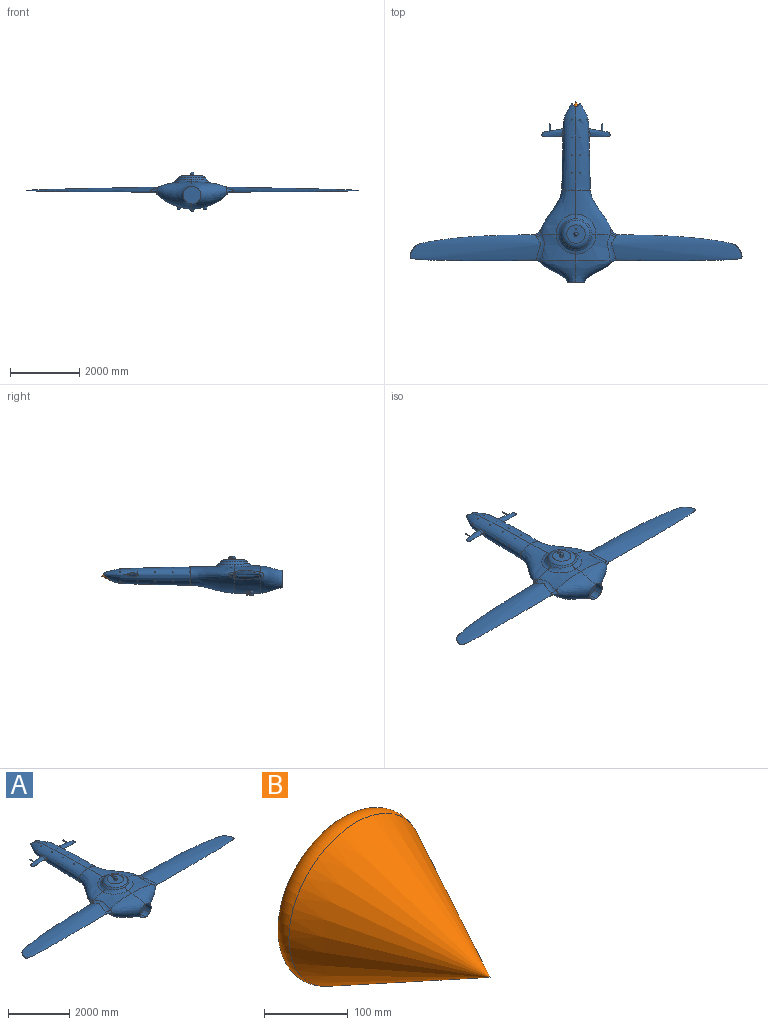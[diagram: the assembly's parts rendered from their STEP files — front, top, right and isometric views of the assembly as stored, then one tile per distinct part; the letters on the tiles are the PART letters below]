
ASSEMBLY  parts=2 mates=1
PART A: 189 faces, bbox 13589.5x5179.7x1155.7 mm
  f0: bspline ~2509.88x526.8mm, area 2318392.8mm2, adj f1,f116,f117,f118,f119,f120,f122,f164
  f1: cylinder r=12.7mm len=106.09mm, axis (0,0,1), area 7616mm2, adj f0,f2,f116,f119
  f2: cylinder r=12.7mm len=254mm, axis (-1,0,0), area 19047.2mm2, adj f1,f3,f114,f115
  f3: cylinder r=12.7mm len=254mm, axis (0,0,1), area 19047.2mm2, adj f2,f4,f112,f113
  f4: cylinder r=12.7mm len=254mm, axis (-1,0,0), area 20268.3mm2, adj f3,f5,f114,f118
  f5: cylinder r=12.7mm len=144.03mm, axis (0,0,1), area 10744mm2, adj f4,f6,f112,f122
  f6: bspline ~1270x1036.44mm, area 1946385.1mm2, adj f5,f7,f89,f90,f91,f92,f93,f94
  f7: bspline ~588.86x581.18mm, area 123308.8mm2, adj f6,f8,f65,f66
  f8: bspline ~588.86x581.18mm, area 123308.8mm2, adj f7,f9,f66,f119
  f9: bspline ~618.36x584.85mm, area 126946.2mm2, adj f8,f10,f65,f66
  f10: extruded ~985.62x762mm, area 505885mm2, adj f9,f11,f54,f89,f119
  f11: bspline ~792.27x241.93mm, area 105491.6mm2, adj f10,f12,f52,f53
  f12: bspline ~183.5x140.7mm, area 9732.5mm2, adj f11,f13,f53,f119
  f13: bspline ~246.9x202.36mm, area 17719.5mm2, adj f12,f14,f53,f119
  f14: bspline ~241.81x196.61mm, area 19710.9mm2, adj f13,f15,f53,f119
  f15: bspline ~211.13x111.05mm, area 6367.3mm2, adj f14,f16,f53,f119
  f16: bspline ~788.4x224mm, area 161750.4mm2, adj f15,f17,f52,f53
  f17: extruded ~995.01x762mm, area 844105.4mm2, adj f16,f18,f35,f54,f94,f119
  f18: sphere r=50.8mm, area 23373mm2, adj f17,f19,f23,f27,f31
  f19: cylinder r=12.7mm len=108.81mm, axis (0,1,0), area 8156.4mm2, adj f18,f20
  f20: torus R=6.35mm, axis (0,-1,0), area 651.3mm2, adj f19,f21
  f21: cylinder r=6.35mm len=110.15mm, axis (0,1,0), area 4270.5mm2, adj f20,f22
  f22: sphere r=50.8mm, area 141.2mm2, adj f21
  f23: cylinder r=12.7mm len=110.32mm, axis (0,1,0), area 8224.9mm2, adj f18,f24
  f24: torus R=6.35mm, axis (0,-1,0), area 651.3mm2, adj f23,f25
  f25: cylinder r=6.35mm len=111.23mm, axis (0,1,0), area 4302.2mm2, adj f24,f26
  f26: sphere r=50.8mm, area 143.8mm2, adj f25
  f27: cylinder r=12.7mm len=104.3mm, axis (0,1,0), area 8323mm2, adj f18,f28
  f28: torus R=6.35mm, axis (0,-1,0), area 651.3mm2, adj f27,f29
  f29: cylinder r=6.35mm len=105.08mm, axis (0,1,0), area 4192.6mm2, adj f28,f30
  f30: sphere r=50.8mm, area 134.4mm2, adj f29
  f31: cylinder r=12.7mm len=105.74mm, axis (0,1,0), area 8437.9mm2, adj f18,f32
  f32: torus R=6.35mm, axis (0,-1,0), area 651.3mm2, adj f31,f33
  f33: cylinder r=6.35mm len=107.99mm, axis (0,1,0), area 4208.2mm2, adj f32,f34
  f34: sphere r=50.8mm, area 136.5mm2, adj f33
  f35: sphere r=50.8mm, area 24215.9mm2, adj f17,f36,f40,f44,f48,f94
  f36: cylinder r=12.7mm len=112.81mm, axis (0,-1,0), area 8336.5mm2, adj f35,f37
  f37: torus R=6.35mm, axis (0,-1,0), area 651.3mm2, adj f36,f38
  f38: cylinder r=6.35mm len=112.95mm, axis (0,-1,0), area 4353.5mm2, adj f37,f39
  f39: sphere r=50.8mm, area 146.5mm2, adj f38
  f40: cylinder r=12.7mm len=112.81mm, axis (0,-1,0), area 8337.9mm2, adj f35,f41
  f41: torus R=6.35mm, axis (0,-1,0), area 651.3mm2, adj f40,f42
  f42: cylinder r=6.35mm len=112.95mm, axis (0,-1,0), area 4353.5mm2, adj f41,f43
  f43: sphere r=50.8mm, area 146.5mm2, adj f42
  f44: cylinder r=12.7mm len=103.69mm, axis (0,-1,0), area 7933.1mm2, adj f35,f45
  f45: torus R=6.35mm, axis (0,-1,0), area 651.3mm2, adj f44,f46
  f46: cylinder r=6.35mm len=106.47mm, axis (0,-1,0), area 4166.3mm2, adj f45,f47
  f47: sphere r=50.8mm, area 132mm2, adj f46
  f48: cylinder r=12.7mm len=103.69mm, axis (0,-1,0), area 7932.9mm2, adj f35,f49
  f49: torus R=6.35mm, axis (0,-1,0), area 651.3mm2, adj f48,f50
  f50: cylinder r=6.35mm len=105.21mm, axis (0,-1,0), area 4164.8mm2, adj f49,f51
  f51: sphere r=50.8mm, area 131.6mm2, adj f50
  f52: bspline ~219.13x194.66mm, area 35350.9mm2, adj f11,f16,f53,f54
  f53: bspline ~6257.94x1180.14mm, area 4844157.5mm2, adj f11,f12,f13,f14,f15,f16,f52
  f54: bspline ~1036.35x785.31mm, area 1162564.2mm2, adj f10,f17,f52,f55,f59,f60
  f55: extruded ~254x186.24mm, area 53098mm2, adj f54,f56,f58,f59
  f56: plane 508x508mm, normal (0,-1,0), area 202688.6mm2, adj f55,f57,f58,f59
  f57: extruded ~426.72x254mm, area 149586.4mm2, adj f56,f58,f59,f60
  f58: extruded ~254x186.24mm, area 53097.8mm2, adj f55,f56,f57,f60
  f59: extruded ~426.72x254mm, area 149583.4mm2, adj f54,f55,f56,f57
  f60: bspline ~1036.35x785.31mm, area 1162564.2mm2, adj f54,f57,f58,f61,f89,f94
  f61: bspline ~219.13x194.66mm, area 35346.5mm2, adj f60,f62,f63,f64
  f62: bspline ~808.62x242.2mm, area 105497.7mm2, adj f61,f63,f89,f90
  f63: bspline ~6257.95x1180.14mm, area 4845672.1mm2, adj f61,f62,f64,f90,f91,f92,f93
  f64: bspline ~782.08x223.3mm, area 161757.5mm2, adj f61,f63,f93,f94
  f65: bspline ~618.36x584.03mm, area 126947.2mm2, adj f7,f9,f66,f89
  f66: sphere r=539.36mm, area 214399.3mm2, adj f7,f8,f9,f65,f67
  f67: torus R=266.46mm, axis (0,0,1), area 311016.1mm2, adj f66,f68
  f68: plane 532.92x532.92mm, normal (0,0,1), area 210384.4mm2, adj f67,f69
  f69: cylinder r=63.5mm len=127mm, axis (0,0,-1), area 86.1mm2, adj f68,f70
  f70: torus R=38.1mm, axis (0,0,1), area 13604.9mm2, adj f69,f71
  f71: plane 76.2x76.2mm, normal (0,0,1), area 257.2mm2, adj f70,f72
  f72: sphere r=50.8mm, area 25095mm2, adj f71,f73,f77,f81,f85
  f73: cylinder r=12.7mm len=106.26mm, axis (0,-1,0), area 8044.5mm2, adj f72,f74
  f74: torus R=6.35mm, axis (0,-1,0), area 651.3mm2, adj f73,f75
  f75: cylinder r=6.35mm len=108.31mm, axis (0,-1,0), area 4234.8mm2, adj f74,f76
  f76: sphere r=50.8mm, area 137.2mm2, adj f75
  f77: cylinder r=12.7mm len=106.26mm, axis (0,-1,0), area 8043.8mm2, adj f72,f78
  f78: torus R=6.35mm, axis (0,-1,0), area 651.3mm2, adj f77,f79
  f79: cylinder r=6.35mm len=108.31mm, axis (0,-1,0), area 4234.8mm2, adj f78,f80
  f80: sphere r=50.8mm, area 137.2mm2, adj f79
  f81: cylinder r=12.7mm len=107.75mm, axis (0,-1,0), area 8105.8mm2, adj f72,f82
  f82: torus R=6.35mm, axis (0,-1,0), area 651.3mm2, adj f81,f83
  f83: cylinder r=6.35mm len=109.39mm, axis (0,-1,0), area 4247.9mm2, adj f82,f84
  f84: sphere r=50.8mm, area 138.5mm2, adj f83
  f85: cylinder r=12.7mm len=107.75mm, axis (0,-1,0), area 8107.9mm2, adj f72,f86
  f86: torus R=6.35mm, axis (0,-1,0), area 651.3mm2, adj f85,f87
  f87: cylinder r=6.35mm len=109.39mm, axis (0,-1,0), area 4248.2mm2, adj f86,f88
  f88: sphere r=50.8mm, area 139.2mm2, adj f87
  f89: extruded ~985.62x762mm, area 505886.1mm2, adj f6,f10,f60,f62,f65
  f90: bspline ~184.63x142.86mm, area 9732.3mm2, adj f6,f62,f63,f91
  f91: bspline ~246.9x202.37mm, area 17719.8mm2, adj f6,f63,f90,f92
  f92: bspline ~241.81x196.61mm, area 19710.7mm2, adj f6,f63,f91,f93
  f93: bspline ~209.2x108.48mm, area 6366.9mm2, adj f6,f63,f64,f92
  f94: extruded ~995.01x762mm, area 838596.6mm2, adj f6,f17,f35,f60,f64,f95
  f95: sphere r=50.8mm, area 23112.9mm2, adj f94,f96,f100,f104,f108
  f96: cylinder r=12.7mm len=107.49mm, axis (0,1,0), area 8096.8mm2, adj f95,f97
  f97: torus R=6.35mm, axis (0,-1,0), area 651.3mm2, adj f96,f98
  f98: cylinder r=6.35mm len=109.2mm, axis (0,1,0), area 4242.8mm2, adj f97,f99
  f99: sphere r=50.8mm, area 139.1mm2, adj f98
  f100: cylinder r=12.7mm len=112.33mm, axis (0,1,0), area 8316.2mm2, adj f95,f101
  f101: torus R=6.35mm, axis (0,-1,0), area 651.3mm2, adj f100,f102
  f102: cylinder r=6.35mm len=112.66mm, axis (0,1,0), area 4344.3mm2, adj f101,f103
  f103: sphere r=50.8mm, area 147.3mm2, adj f102
  f104: cylinder r=12.7mm len=107.56mm, axis (0,1,0), area 8583.2mm2, adj f95,f105
  f105: torus R=6.35mm, axis (0,-1,0), area 651.3mm2, adj f104,f106
  f106: cylinder r=6.35mm len=109.38mm, axis (0,1,0), area 4248.1mm2, adj f105,f107
  f107: sphere r=50.8mm, area 139.5mm2, adj f106
  f108: cylinder r=12.7mm len=102.97mm, axis (0,1,0), area 7903mm2, adj f95,f109
  f109: torus R=6.35mm, axis (0,-1,0), area 651.3mm2, adj f108,f110
  f110: cylinder r=6.35mm len=105.95mm, axis (0,1,0), area 4151.9mm2, adj f109,f111
  f111: sphere r=50.8mm, area 132.5mm2, adj f110
  f112: cylinder r=12.7mm len=268.02mm, axis (-1,0,0), area 20180.1mm2, adj f3,f5,f6,f122
  f113: cylinder r=12.7mm len=207.13mm, axis (-1,0,0), area 14835.5mm2, adj f3,f6,f115,f122
  f114: cylinder r=12.7mm len=254mm, axis (0,0,1), area 19047.2mm2, adj f2,f4,f116,f117
  f115: cylinder r=12.7mm len=106.09mm, axis (0,0,1), area 7616mm2, adj f2,f6,f113,f122
  f116: cylinder r=12.7mm len=207.13mm, axis (-1,0,0), area 14904.7mm2, adj f0,f1,f114,f119
  f117: cylinder r=12.7mm len=268.02mm, axis (-1,0,0), area 20180.1mm2, adj f0,f114,f118,f119
  f118: cylinder r=12.7mm len=144.03mm, axis (0,0,1), area 10744mm2, adj f0,f4,f117,f119
  f119: bspline ~1270x1036.44mm, area 1946422mm2, adj f0,f1,f6,f8,f10,f12,f13,f14
  f120: cylinder r=127mm len=404.44mm, axis (0,1,0), area 238128.3mm2, adj f0,f121,f122
  f121: plane 254x254mm, normal (0,1,0), area 50670.7mm2, adj f120
  f122: bspline ~2512.68x526.8mm, area 2314098.8mm2, adj f0,f5,f6,f112,f113,f115,f120,f123
  f123: cylinder r=12.7mm len=237.09mm, axis (-1,0,0), area 17739.1mm2, adj f122,f124,f159
  f124: cylinder r=12.7mm len=254mm, axis (0,0,1), area 19047.2mm2, adj f123,f125,f127,f154
  f125: cylinder r=12.7mm len=254mm, axis (-1,0,0), area 19047.2mm2, adj f124,f126,f158,f165
  f126: cylinder r=12.7mm len=254mm, axis (0,0,1), area 19047.2mm2, adj f125,f127,f168,f183
  f127: cylinder r=12.7mm len=254mm, axis (-1,0,0), area 19047.2mm2, adj f124,f126,f159,f187
  f128: cylinder r=12.7mm len=258.69mm, axis (-1,0,0), area 19559.6mm2, adj f122,f129,f163
  f129: cylinder r=12.7mm len=254mm, axis (0,0,1), area 19047.2mm2, adj f128,f130,f132,f138
  f130: cylinder r=12.7mm len=254mm, axis (-1,0,0), area 19047.2mm2, adj f129,f131,f162,f167
  f131: cylinder r=12.7mm len=254mm, axis (0,0,1), area 19047.2mm2, adj f130,f132,f169,f171
  f132: cylinder r=12.7mm len=254mm, axis (-1,0,0), area 19047.2mm2, adj f129,f131,f163,f185
  f133: cylinder r=12.7mm len=107.69mm, axis (-1,0,0), area 6456.4mm2, adj f122,f134,f156
  f134: cylinder r=12.7mm len=254mm, axis (0,0,1), area 19047.2mm2, adj f133,f135,f137,f148
  f135: cylinder r=12.7mm len=254mm, axis (-1,0,0), area 19047.2mm2, adj f134,f136,f156,f164
  f136: cylinder r=12.7mm len=254mm, axis (0,0,1), area 19047.2mm2, adj f135,f137,f170,f181
  f137: cylinder r=12.7mm len=254mm, axis (-1,0,0), area 19047.2mm2, adj f134,f136,f157,f188
  f138: cylinder r=12.7mm len=202.09mm, axis (-1,0,0), area 14521.6mm2, adj f122,f129,f162
  f139: bspline ~295.03x108.05mm, area 31421mm2, adj f122,f140,f146,f147
  f140: bspline ~1015.9x358.87mm, area 200607.7mm2, adj f139,f141,f142,f146,f147
  f141: torus R=7.62mm, axis (0,1,0), area 1528.2mm2, adj f140,f142
  f142: cylinder r=12.7mm len=255.27mm, axis (0,-1,0), area 17606.1mm2, adj f140,f141,f143
  f143: torus R=6.35mm, axis (0,1,0), area 651.3mm2, adj f142,f144
  f144: cylinder r=6.35mm len=139.7mm, axis (0,-1,0), area 5573.8mm2, adj f143,f145
  f145: plane 12.7x12.7mm, normal (0,1,0), area 126.7mm2, adj f144
  f146: bspline ~56.61x55.15mm, area 1675mm2, adj f122,f139,f140,f147
  f147: bspline ~59.44x54.97mm, area 1492mm2, adj f122,f139,f140,f146
  f148: cylinder r=12.7mm len=205.31mm, axis (-1,0,0), area 14745.6mm2, adj f122,f134,f157
  f149: cylinder r=12.7mm len=189.58mm, axis (-1,0,0), area 13488mm2, adj f122,f150,f160
  f150: cylinder r=12.7mm len=254mm, axis (0,0,1), area 19047.2mm2, adj f149,f151,f153,f155
  f151: cylinder r=12.7mm len=254mm, axis (-1,0,0), area 19047.2mm2, adj f150,f152,f160,f166
  f152: cylinder r=12.7mm len=254mm, axis (0,0,1), area 19047.2mm2, adj f151,f153,f182,f184
  f153: cylinder r=12.7mm len=254mm, axis (-1,0,0), area 19047.2mm2, adj f150,f152,f161,f186
  f154: cylinder r=12.7mm len=164.58mm, axis (-1,0,0), area 11356.2mm2, adj f122,f124,f158
  f155: cylinder r=12.7mm len=249.54mm, axis (-1,0,0), area 18836mm2, adj f122,f150,f161
  f156: cylinder r=12.7mm len=48.26mm, axis (0,0,1), area 3275.4mm2, adj f122,f133,f135
  f157: cylinder r=12.7mm len=87.14mm, axis (0,0,1), area 6446.9mm2, adj f122,f137,f148
  f158: cylinder r=12.7mm len=82.06mm, axis (0,0,1), area 5971.9mm2, adj f122,f125,f154
  f159: cylinder r=12.7mm len=116.5mm, axis (0,0,1), area 8789.2mm2, adj f122,f123,f127
  f160: cylinder r=12.7mm len=98.91mm, axis (0,0,1), area 7316.3mm2, adj f122,f149,f151
  f161: cylinder r=12.7mm len=133.64mm, axis (0,0,1), area 10157mm2, adj f122,f153,f155
  f162: cylinder r=12.7mm len=106.77mm, axis (0,0,1), area 7943.9mm2, adj f122,f130,f138
  f163: cylinder r=12.7mm len=142.71mm, axis (0,0,1), area 10881.3mm2, adj f122,f128,f132
  f164: cylinder r=12.7mm len=39.21mm, axis (0,0,1), area 2553mm2, adj f0,f135,f170
  f165: cylinder r=12.7mm len=75.14mm, axis (0,0,1), area 5419.9mm2, adj f0,f125,f183
  f166: cylinder r=12.7mm len=92.76mm, axis (0,0,1), area 6825.7mm2, adj f0,f151,f182
  f167: cylinder r=12.7mm len=100.52mm, axis (0,0,1), area 7445mm2, adj f0,f130,f171
  f168: cylinder r=12.7mm len=237.99mm, axis (-1,0,0), area 17808.6mm2, adj f0,f126,f187
  f169: cylinder r=12.7mm len=260.83mm, axis (-1,0,0), area 19725.9mm2, adj f0,f131,f185
  f170: cylinder r=12.7mm len=107.71mm, axis (-1,0,0), area 6528.5mm2, adj f0,f136,f164
  f171: cylinder r=12.7mm len=203.55mm, axis (-1,0,0), area 14698.4mm2, adj f0,f131,f167
  f172: bspline ~293.49x107.99mm, area 31238.3mm2, adj f0,f173,f179,f180
  f173: bspline ~1015.9x358.87mm, area 199700.6mm2, adj f172,f174,f175,f179,f180
  f174: torus R=7.62mm, axis (0,1,0), area 0mm2, adj f173,f175
  f175: cylinder r=12.7mm len=255.27mm, axis (0,-1,0), area 17599.9mm2, adj f173,f174,f176
  f176: torus R=6.35mm, axis (0,1,0), area 651.3mm2, adj f175,f177
  f177: cylinder r=6.35mm len=139.7mm, axis (0,-1,0), area 5573.8mm2, adj f176,f178
  f178: plane 12.7x12.7mm, normal (0,1,0), area 126.7mm2, adj f177
  f179: bspline ~59.53x55.14mm, area 1495.2mm2, adj f0,f172,f173,f180
  f180: bspline ~56.95x55.34mm, area 1698.5mm2, adj f0,f172,f173,f179
  f181: cylinder r=12.7mm len=205.34mm, axis (-1,0,0), area 14748.2mm2, adj f0,f136,f188
  f182: cylinder r=12.7mm len=190.92mm, axis (-1,0,0), area 13656.4mm2, adj f0,f152,f166
  f183: cylinder r=12.7mm len=165.14mm, axis (-1,0,0), area 11467.3mm2, adj f0,f126,f165
  f184: cylinder r=12.7mm len=251.55mm, axis (-1,0,0), area 18992.9mm2, adj f0,f152,f186
  f185: cylinder r=12.7mm len=139.91mm, axis (0,0,1), area 10588mm2, adj f0,f132,f169
  f186: cylinder r=12.7mm len=131.64mm, axis (0,0,1), area 9928.3mm2, adj f0,f153,f184
  f187: cylinder r=12.7mm len=114.1mm, axis (0,0,1), area 8528.6mm2, adj f0,f127,f168
  f188: cylinder r=12.7mm len=82.45mm, axis (0,0,1), area 6003mm2, adj f0,f137,f181
PART B: 3 faces, bbox 249.4x254x249.4 mm
  f0: plane 192.35x192.35mm, normal (0,1,0), area 29059.4mm2, adj f2
  f1: cone r=127mm half-angle=26.6deg, axis (0,1,0), area 90042mm2, adj f2
  f2: torus R=96.18mm, axis (0,-1,0), area 26720mm2, adj f0,f1
PLACE A t=(1095.01,6021.71,-1067.82)mm
PLACE B rot(axis=(0,0,1),180deg) t=(1095.01,5666.38,-1118.62)mm
MATE fastened B.f1 <-> A.f120  axis (0,-1,0) through (1095.01,5666.38,-1118.62)mm
